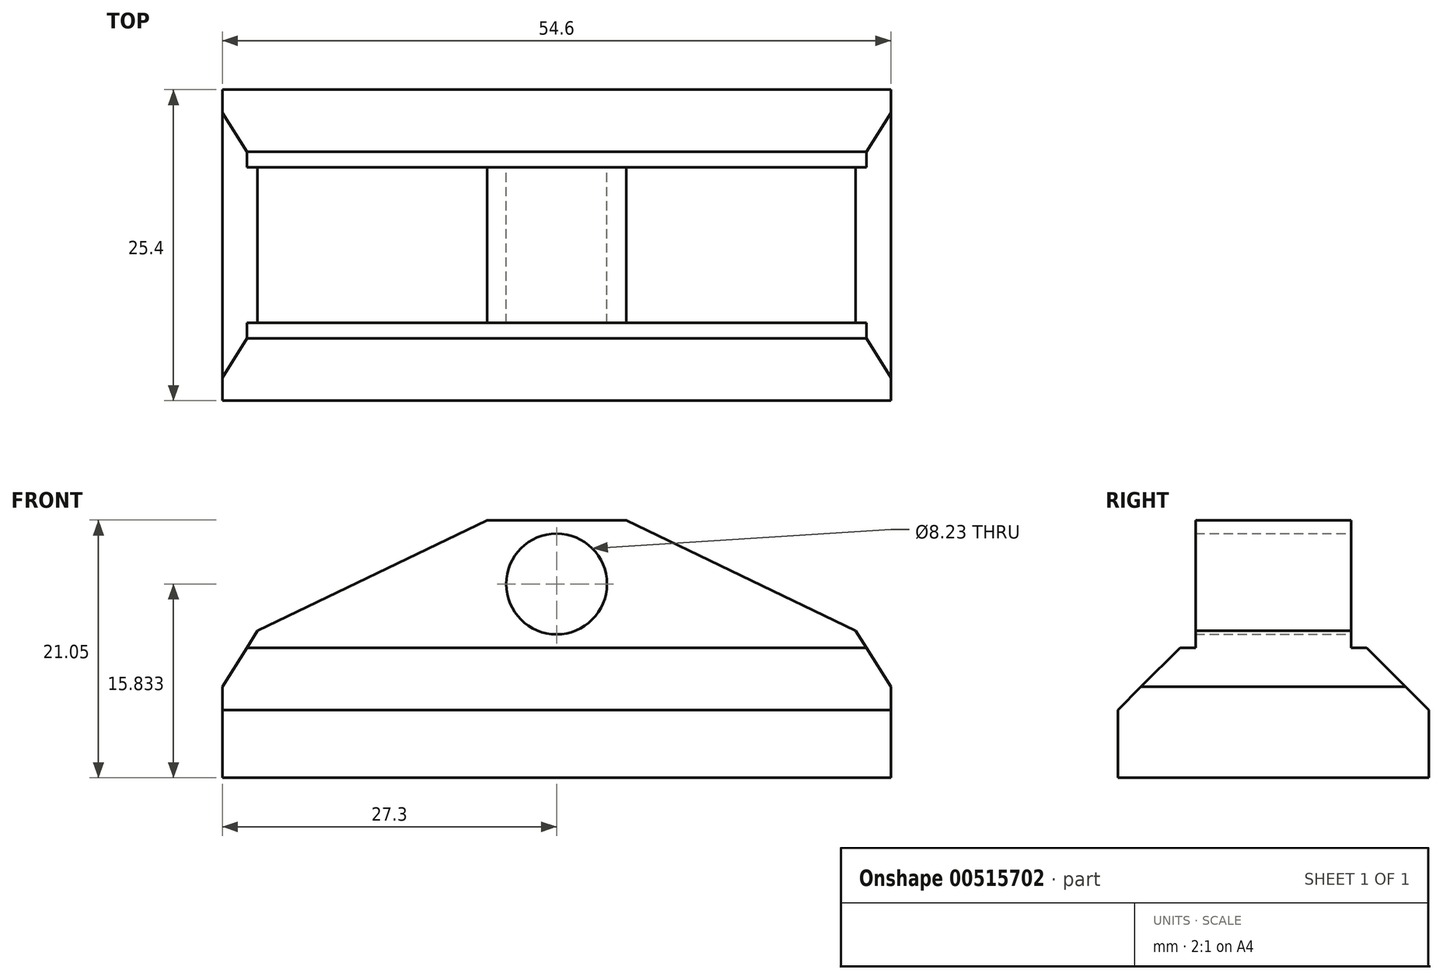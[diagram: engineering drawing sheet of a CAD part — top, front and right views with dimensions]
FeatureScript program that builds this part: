
annotation { "Feature Type Name" : "Feature", "Feature Type Description" : "" }
export const myFeature = defineFeature(function(context is Context, id is Id, definition is map)
    precondition{}
    {
        {
            var Q0;
            Q0=qCreatedBy(makeId("Front.planeOp"),FACE);
            var sketch = newSketch(context, id + "F0", { "sketchPlane" : qUnion([Q0])});
            skLineSegment(sketch, "E0.bottom", {"start": v(-27.3, 5.3) * mm, "end": v(27.3, 5.3) * mm});
            skLineSegment(sketch, "E0.top", {"start": v(-27.3, -5.3) * mm, "end": v(27.3, -5.3) * mm});
            skLineSegment(sketch, "E0.left", {"start": v(-27.3, 5.3) * mm, "end": v(-27.3, -5.3) * mm});
            skLineSegment(sketch, "E0.right", {"start": v(27.3, 5.3) * mm, "end": v(27.3, -5.3) * mm});
            skPoint(sketch, "E0.middle", {"position": v(0, 0) * mm});
            skLineSegment(sketch, "E1", {"start": v(0, 15.74) * mm, "end": v(-5.69, 15.74) * mm});
            skPoint(sketch, "E1.startSnap0", {"position": v(0, 5.3) * mm});
            skLineSegment(sketch, "E2", {"start": v(-5.69, 15.74) * mm, "end": v(0, 15.74) * mm});
            skLineSegment(sketch, "E3", {"start": v(0, 15.74) * mm, "end": v(5.69, 15.74) * mm});
            skLineSegment(sketch, "E4", {"start": v(5.69, 15.74) * mm, "end": v(27.3, 5.3) * mm});
            skLineSegment(sketch, "E5", {"start": v(-5.69, 15.74) * mm, "end": v(-27.3, 5.3) * mm});
            skCircle(sketch, "E6", {"center": v(0, 10.52) * mm, "radius": 2.59 * mm});
            skPoint(sketch, "E6.centerSnap0", {"position": v(-16.5, 10.52) * mm});
            skCircle(sketch, "E7", {"center": v(0, 10.52) * mm, "radius": 4.12 * mm});
            skSolve(sketch);
        }
        {
            var Q0;
            Q0=makeQuery(id+"F0.imprint","IMPRINT",FACE,{"disambiguationData":[TD([[makeQuery(id+"F0.imprint","IMPRINT",EDGE,{"derivedFrom":sQuery(id+"F0.wireOp",EDGE,"E0.bottom")}),1.0]])]});
            extrude(context, id + "F1", {"entities" : qUnion([Q0]), "endBound" : BoundingType.SYMMETRIC, "depth" : 12.7 * mm, "offsetDistance" : 25.4 * mm});
        }
        {
            var Q0;
            Q0=makeQuery(id+"F0.imprint","IMPRINT",FACE,{"disambiguationData":[TD([[makeQuery(id+"F0.imprint","IMPRINT",EDGE,{"derivedFrom":sQuery(id+"F0.wireOp",EDGE,"E0.bottom")}),-1.0]])]});
            extrude(context, id + "F2", {"entities" : qUnion([Q0]), "operationType" : NewBodyOperationType.ADD, "endBound" : BoundingType.SYMMETRIC, "depth" : 25.4 * mm, "offsetDistance" : 25.4 * mm});
        }
        {
            var Q0;
            Q0=makeQuery(id+"F2.opExtrude","CAP_EDGE",EDGE,{"disambiguationData":[OSD([sQuery(id+"F0.wireOp",EDGE,"E0.bottom")])],"isStart":false});
            var Q1;
            Q1=makeQuery(id+"F2.opExtrude","CAP_EDGE",EDGE,{"disambiguationData":[OSD([sQuery(id+"F0.wireOp",EDGE,"E0.bottom")])],"isStart":true});
            var Q2;
            {var subQ0=sQuery(id+"F0.wireOp",EDGE,"E5");var subQ1=sQuery(id+"F0.wireOp",EDGE,"E0.left");var subQ2=sQuery(id+"F0.wireOp",EDGE,"E0.bottom");Q2=makeQuery(id+"F2.boolean.opBoolean","MERGE",EDGE,{"derivedFrom":[makeQuery(id+"F1.opExtrude","SWEPT_EDGE",EDGE,{"disambiguationData":[OSD([subQ2,subQ1,subQ0])]}),makeQuery(id+"F2.opExtrude","SWEPT_EDGE",EDGE,{"disambiguationData":[OSD([subQ2,subQ1,subQ0])]})]});}
            var Q3;
            {var subQ0=sQuery(id+"F0.wireOp",EDGE,"E4");var subQ1=sQuery(id+"F0.wireOp",EDGE,"E0.right");var subQ2=sQuery(id+"F0.wireOp",EDGE,"E0.bottom");Q3=makeQuery(id+"F2.boolean.opBoolean","MERGE",EDGE,{"derivedFrom":[makeQuery(id+"F1.opExtrude","SWEPT_EDGE",EDGE,{"disambiguationData":[OSD([subQ2,subQ1,subQ0])]}),makeQuery(id+"F2.opExtrude","SWEPT_EDGE",EDGE,{"disambiguationData":[OSD([subQ2,subQ1,subQ0])]})]});}
            chamfer(context, id + "F3", {"entities" : qUnion([Q0, Q1, Q2, Q3]), "width" : 5.08 * mm, "tangentPropagation" : true});
        }
    });
